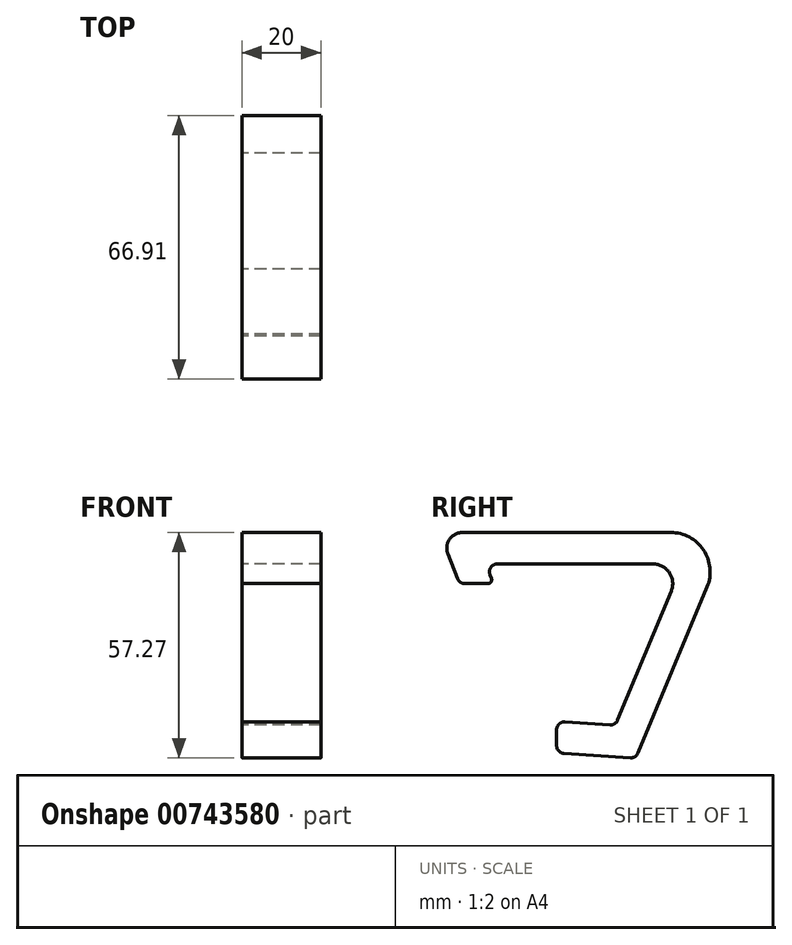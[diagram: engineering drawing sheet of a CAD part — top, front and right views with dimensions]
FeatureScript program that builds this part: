
annotation { "Feature Type Name" : "Feature", "Feature Type Description" : "" }
export const myFeature = defineFeature(function(context is Context, id is Id, definition is map)
    precondition{}
    {
        {
            var Q0;
            Q0=qCreatedBy(makeId("Right.planeOp"),FACE);
            var sketch = newSketch(context, id + "F0", { "sketchPlane" : qUnion([Q0])});
            skLineSegment(sketch, "E0", {"start": v(-35.2, 0) * mm, "end": v(4.35, 0) * mm});
            skLineSegment(sketch, "E1", {"start": v(8.97, -6.92) * mm, "end": v(-4.64, -39.68) * mm});
            skLineSegment(sketch, "E2", {"start": v(-6.62, -40.9) * mm, "end": v(-18.02, -40.14) * mm});
            skLineSegment(sketch, "E3", {"start": v(-20.15, -42.14) * mm, "end": v(-20.15, -46.15) * mm});
            skLineSegment(sketch, "E4", {"start": v(-18.29, -48.14) * mm, "end": v(-1.43, -49.27) * mm});
            skLineSegment(sketch, "E5", {"start": v(0.55, -48.04) * mm, "end": v(18.08, -5.84) * mm});
            skLineSegment(sketch, "E6", {"start": v(8.85, 8) * mm, "end": v(-44.06, 8) * mm});
            skLineSegment(sketch, "E7", {"start": v(-47.78, 2.51) * mm, "end": v(-45.27, -3.74) * mm});
            skLineSegment(sketch, "E8", {"start": v(-43.42, -5) * mm, "end": v(-37.63, -5) * mm});
            skLineSegment(sketch, "E9", {"start": v(-36.7, -3.63) * mm, "end": v(-37.06, -2.74) * mm});
            skPoint(sketch, "E10.visualSharp", {"position": v(-49.97, 8) * mm});
            skArc(sketch, "E10.filletArc", {"start": v(-44.06, 8) * mm, "mid": v(-47.37, 6.24) * mm, "end": v(-47.78, 2.51) * mm});
            skPoint(sketch, "E11.visualSharp", {"position": v(23.83, 8) * mm});
            skArc(sketch, "E11.filletArc", {"start": v(18.08, -5.84) * mm, "mid": v(17.17, 3.55) * mm, "end": v(8.85, 8) * mm});
            skPoint(sketch, "E12.visualSharp", {"position": v(-38.15, 0) * mm});
            skArc(sketch, "E12.filletArc", {"start": v(-35.2, 0) * mm, "mid": v(-36.86, -0.88) * mm, "end": v(-37.06, -2.74) * mm});
            skPoint(sketch, "E13.visualSharp", {"position": v(11.85, 0) * mm});
            skArc(sketch, "E13.filletArc", {"start": v(8.97, -6.92) * mm, "mid": v(8.51, -2.22) * mm, "end": v(4.35, 0) * mm});
            skPoint(sketch, "E14.visualSharp", {"position": v(-5.19, -41) * mm});
            skArc(sketch, "E14.filletArc", {"start": v(-6.62, -40.9) * mm, "mid": v(-5.43, -40.6) * mm, "end": v(-4.64, -39.68) * mm});
            skPoint(sketch, "E15.visualSharp", {"position": v(0, -49.36) * mm});
            skArc(sketch, "E15.filletArc", {"start": v(-1.43, -49.27) * mm, "mid": v(-0.24, -48.97) * mm, "end": v(0.55, -48.04) * mm});
            skPoint(sketch, "E16.visualSharp", {"position": v(-20.15, -48.02) * mm});
            skArc(sketch, "E16.filletArc", {"start": v(-20.15, -46.15) * mm, "mid": v(-19.62, -47.51) * mm, "end": v(-18.29, -48.14) * mm});
            skPoint(sketch, "E17.visualSharp", {"position": v(-44.77, -5) * mm});
            skArc(sketch, "E17.filletArc", {"start": v(-45.27, -3.74) * mm, "mid": v(-44.54, -4.66) * mm, "end": v(-43.42, -5) * mm});
            skPoint(sketch, "E18.visualSharp", {"position": v(-20.15, -40) * mm});
            skArc(sketch, "E18.filletArc", {"start": v(-18.02, -40.14) * mm, "mid": v(-19.52, -40.68) * mm, "end": v(-20.15, -42.14) * mm});
            skPoint(sketch, "E19.visualSharp", {"position": v(-36.15, -5) * mm});
            skArc(sketch, "E19.filletArc", {"start": v(-37.63, -5) * mm, "mid": v(-36.8, -4.56) * mm, "end": v(-36.7, -3.63) * mm});
            skSolve(sketch);
        }
        {
            var Q0;
            Q0 = qSketchRegion(id + "F0", true);
            extrude(context, id + "F1", {"entities" : qUnion([Q0]), "depth" : 20 * mm, "offsetDistance" : 25.4 * mm});
        }
    });
